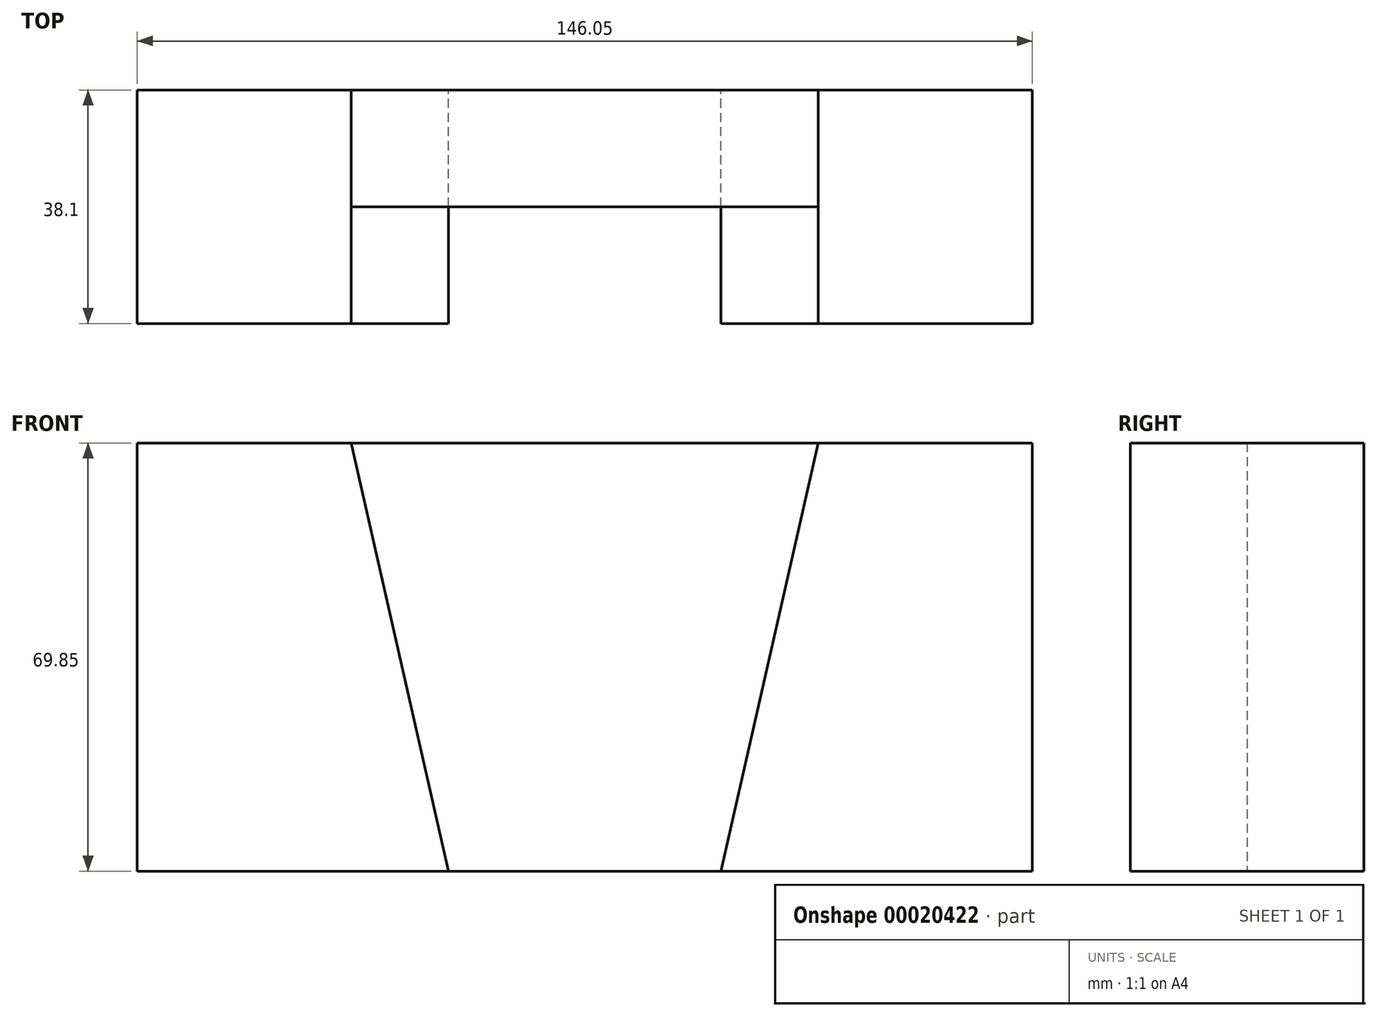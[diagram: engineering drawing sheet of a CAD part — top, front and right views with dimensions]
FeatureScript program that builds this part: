
annotation { "Feature Type Name" : "Feature", "Feature Type Description" : "" }
export const myFeature = defineFeature(function(context is Context, id is Id, definition is map)
    precondition{}
    {
        {
            var Q0;
            Q0=qCreatedBy(makeId("Front.planeOp"),FACE);
            var sketch = newSketch(context, id + "F0", { "sketchPlane" : qUnion([Q0])});
            skLineSegment(sketch, "E0", {"start": v(74.93, -56.12) * mm, "end": v(74.93, 13.73) * mm});
            skLineSegment(sketch, "E1", {"start": v(74.93, -56.12) * mm, "end": v(24.13, -56.12) * mm});
            skLineSegment(sketch, "E2", {"start": v(24.13, -56.12) * mm, "end": v(-20.32, -56.12) * mm});
            skLineSegment(sketch, "E3", {"start": v(-20.32, -56.12) * mm, "end": v(-71.12, -56.12) * mm});
            skLineSegment(sketch, "E4", {"start": v(-71.12, -56.12) * mm, "end": v(-71.12, 13.73) * mm});
            skLineSegment(sketch, "E5", {"start": v(-71.12, 13.73) * mm, "end": v(-36.2, 13.73) * mm});
            skLineSegment(sketch, "E6", {"start": v(-36.2, 13.73) * mm, "end": v(-20.32, -56.12) * mm});
            skLineSegment(sketch, "E7", {"start": v(74.93, 13.73) * mm, "end": v(40, 13.73) * mm});
            skLineSegment(sketch, "E8", {"start": v(40, 13.73) * mm, "end": v(24.13, -56.12) * mm});
            skLineSegment(sketch, "E9", {"start": v(-36.2, 13.73) * mm, "end": v(40, 13.73) * mm});
            skSolve(sketch);
        }
        {
            var Q0;
            Q0=makeQuery(id+"F0.imprint","IMPRINT",FACE,{"disambiguationData":[TD([[makeQuery(id+"F0.imprint","IMPRINT",EDGE,{"derivedFrom":sQuery(id+"F0.wireOp",EDGE,"E3")}),-1.0]])]});
            extrude(context, id + "F1", {"entities" : qUnion([Q0]), "depth" : 38.1 * mm});
        }
        {
            var Q0;
            Q0=makeQuery(id+"F0.imprint","IMPRINT",FACE,{"disambiguationData":[TD([[makeQuery(id+"F0.imprint","IMPRINT",EDGE,{"derivedFrom":sQuery(id+"F0.wireOp",EDGE,"E0")}),1.0]])]});
            extrude(context, id + "F2", {"entities" : qUnion([Q0]), "depth" : 38.1 * mm});
        }
        {
            var Q0;
            Q0=makeQuery(id+"F0.imprint","IMPRINT",FACE,{"disambiguationData":[TD([[makeQuery(id+"F0.imprint","IMPRINT",EDGE,{"derivedFrom":sQuery(id+"F0.wireOp",EDGE,"E2")}),-1.0]])]});
            extrude(context, id + "F3", {"entities" : qUnion([Q0]), "depth" : 19.05 * mm});
        }
    });
